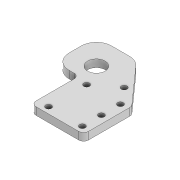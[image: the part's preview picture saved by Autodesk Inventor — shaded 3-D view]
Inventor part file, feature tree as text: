
AUTODESK INVENTOR PART (.ipt)
format: ipt  version: 2022 (Build 260153000, 153)  size: 163,328 bytes
history: native  units: mm
features: fillet x2, sketch x2, extrude x1, projected_geometry x1
ambient origin geometry x8: Origin, YZ Plane, XZ Plane, XY Plane, X Axis, Y Axis, Z Axis, Center Point
bodies: Solid1 (feature_tree)
feature tree (6):
  extrude  "Extrusion1"  Depth=21.0mm
  fillet  "Fillet1"  Radius=1.0mm
  fillet  "Fillet2"  Radius=7.0mm
  sketch  "Sketch2"  dims[d4=16.0mm d5=10.0mm d6=10.0mm d8=6.0mm d9=2.3mm d10=1.5mm d11=2.3mm d12=3.0mm d13=4.5mm d14=1.5mm d15=2.3mm d16=1.5mm d17=3.0mm d18=2.3mm d19=4.5mm d20=1.5mm d21=3.0mm d22=0.0mm d23=2.0mm d24=6.0mm d25=2.3mm d26=14.1mm d27=8.0mm d28=2.3mm d29=3.0mm]
  sketch  "Sketch1"  dims[d0=9.1mm d1=21.0mm d2=1.0mm d3=7.0mm]
  projected_geometry  "Projected Loop1"
